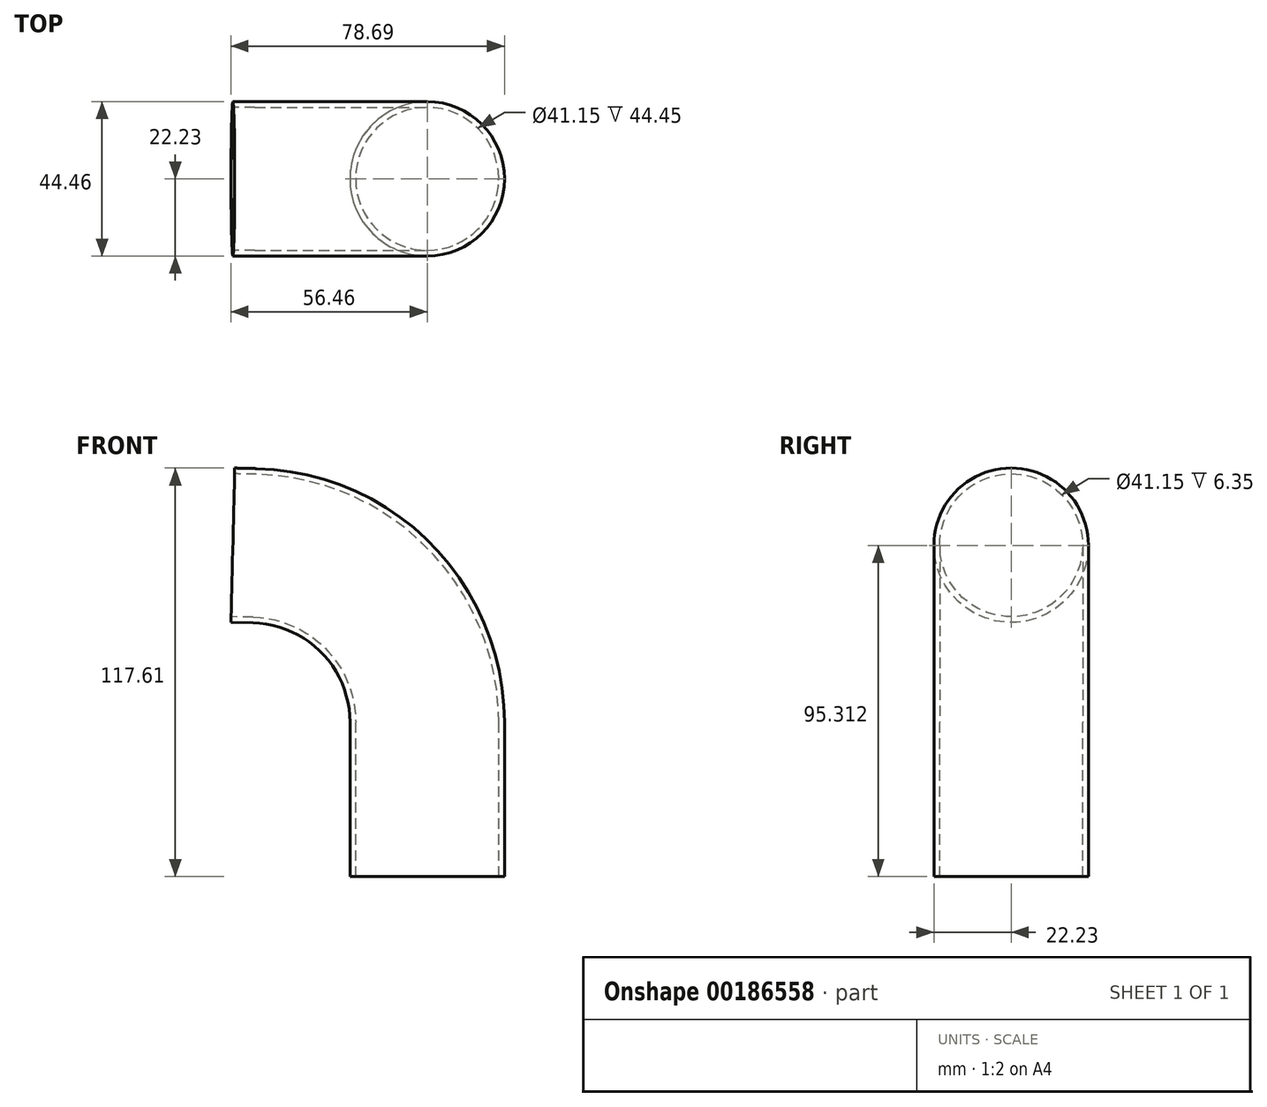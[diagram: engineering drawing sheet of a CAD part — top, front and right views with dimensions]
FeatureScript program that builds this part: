
annotation { "Feature Type Name" : "Feature", "Feature Type Description" : "" }
export const myFeature = defineFeature(function(context is Context, id is Id, definition is map)
    precondition{}
    {
        {
            var Q0;
            Q0=qCreatedBy(makeId("Front.planeOp"),FACE);
            var sketch = newSketch(context, id + "F0", { "sketchPlane" : qUnion([Q0])});
            skPoint(sketch, "E0.visualSharp", {"position": v(-20.12, 82.36) * mm});
            skLineSegment(sketch, "E1", {"start": v(0, 0) * mm, "end": v(0, 44.45) * mm});
            skLineSegment(sketch, "E2", {"start": v(-55.92, 95.39) * mm, "end": v(-49.57, 95.24) * mm});
            skPoint(sketch, "E3.visualSharp", {"position": v(0, 94.04) * mm});
            skArc(sketch, "E3.filletArc", {"start": v(0, 44.45) * mm, "mid": v(-14.45, 79.93) * mm, "end": v(-49.57, 95.24) * mm});
            skSolve(sketch);
        }
        {
            var Q0;
            Q0=qCreatedBy(makeId("Top.planeOp"),FACE);
            var sketch = newSketch(context, id + "F1", { "sketchPlane" : qUnion([Q0])});
            skCircle(sketch, "E4", {"center": v(0, 0) * mm, "radius": 22.23 * mm});
            skCircle(sketch, "E5", {"center": v(0, 0) * mm, "radius": 20.57 * mm});
            skSolve(sketch);
        }
        {
            var Q0;
            Q0 = qSketchRegion(id + "F1", true);
            var Q1;
            Q1 = qConstructionFilter(qBodyType(qCreatedBy(id + "F0" ,EDGE), BodyType.WIRE), ConstructionObject.NO);
            sweep(context, id + "F2", {"profiles" : qUnion([Q0]), "path" : qUnion([Q1])});
        }
    });
